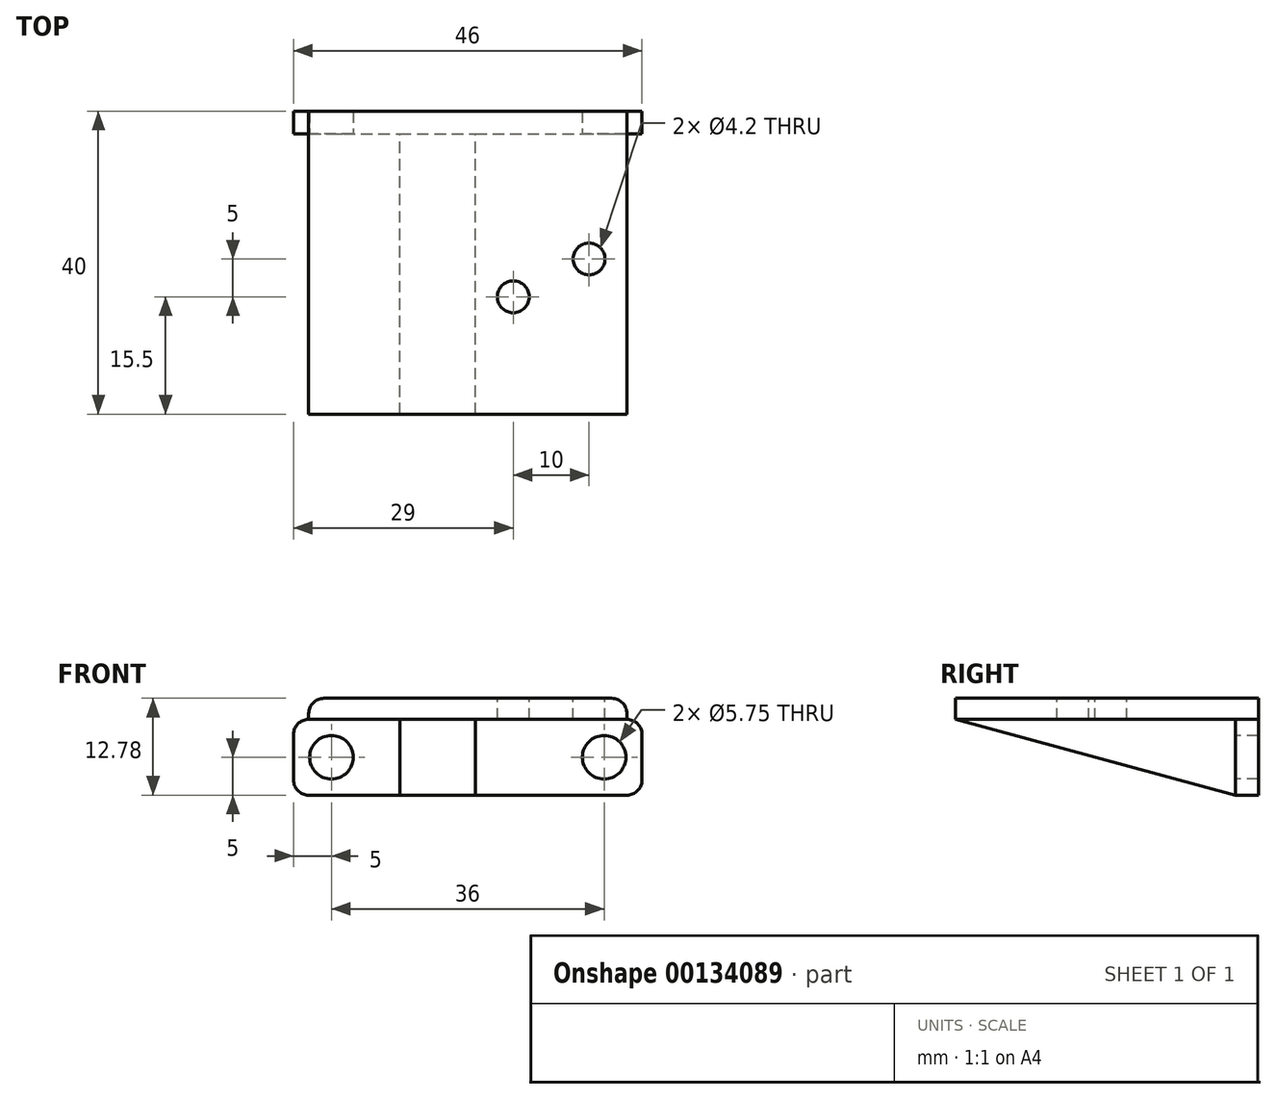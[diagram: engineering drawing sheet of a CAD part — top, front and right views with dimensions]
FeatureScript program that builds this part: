
annotation { "Feature Type Name" : "Feature", "Feature Type Description" : "" }
export const myFeature = defineFeature(function(context is Context, id is Id, definition is map)
    precondition{}
    {
        {
            var Q0;
            Q0=qCreatedBy(makeId("Front.planeOp"),FACE);
            var sketch = newSketch(context, id + "F0", { "sketchPlane" : qUnion([Q0])});
            skLineSegment(sketch, "E0.bottom", {"start": v(-21, 0) * mm, "end": v(21, 0) * mm});
            skLineSegment(sketch, "E0.top", {"start": v(-21, -10) * mm, "end": v(21, -10) * mm});
            skLineSegment(sketch, "E0.left", {"start": v(-23, -2) * mm, "end": v(-23, -8) * mm});
            skLineSegment(sketch, "E0.right", {"start": v(23, -2) * mm, "end": v(23, -8) * mm});
            skLineSegment(sketch, "E1", {"start": v(-23, 0) * mm, "end": v(0, 0) * mm, "construction": true});
            skLineSegment(sketch, "E2", {"start": v(0, 0) * mm, "end": v(23, 0) * mm, "construction": true});
            skPoint(sketch, "E3.visualSharp", {"position": v(-23, 0) * mm});
            skArc(sketch, "E3.filletArc", {"start": v(-21, 0) * mm, "mid": v(-22.41, -0.59) * mm, "end": v(-23, -2) * mm});
            skPoint(sketch, "E4.visualSharp", {"position": v(23, 0) * mm});
            skArc(sketch, "E4.filletArc", {"start": v(23, -2) * mm, "mid": v(22.41, -0.59) * mm, "end": v(21, 0) * mm});
            skPoint(sketch, "E5.visualSharp", {"position": v(23, -10) * mm});
            skArc(sketch, "E5.filletArc", {"start": v(21, -10) * mm, "mid": v(22.41, -9.41) * mm, "end": v(23, -8) * mm});
            skPoint(sketch, "E6.visualSharp", {"position": v(-23, -10) * mm});
            skArc(sketch, "E6.filletArc", {"start": v(-23, -8) * mm, "mid": v(-22.41, -9.41) * mm, "end": v(-21, -10) * mm});
            skPoint(sketch, "E7.endSnap0", {"position": v(0, -10) * mm});
            skSolve(sketch);
        }
        {
            var Q0;
            Q0 = qSketchRegion(id + "F0", true);
            extrude(context, id + "F1", {"entities" : qUnion([Q0]), "depth" : 3 * mm});
        }
        {
            var Q0;
            Q0=makeQuery(id+"F1.opExtrude","CAP_FACE",FACE,{"disambiguationData":[OSD([sQuery(id+"F0.wireOp",EDGE,"E0.bottom"),sQuery(id+"F0.wireOp",EDGE,"E0.top"),sQuery(id+"F0.wireOp",EDGE,"E0.left"),sQuery(id+"F0.wireOp",EDGE,"E0.right"),sQuery(id+"F0.wireOp",EDGE,"E3.filletArc"),sQuery(id+"F0.wireOp",EDGE,"E4.filletArc"),sQuery(id+"F0.wireOp",EDGE,"E5.filletArc"),sQuery(id+"F0.wireOp",EDGE,"E6.filletArc")])],"isStart":false});
            var sketch = newSketch(context, id + "F2", { "sketchPlane" : qUnion([Q0])});
            skLineSegment(sketch, "E8", {"start": v(0, 0) * mm, "end": v(0, -5) * mm, "construction": true});
            skLineSegment(sketch, "E9", {"start": v(0, -5) * mm, "end": v(0, -10) * mm, "construction": true});
            skLineSegment(sketch, "E10", {"start": v(-18, -5) * mm, "end": v(0, -5) * mm, "construction": true});
            skLineSegment(sketch, "E11", {"start": v(0, -5) * mm, "end": v(18, -5) * mm, "construction": true});
            skCircle(sketch, "E12", {"center": v(-18, -5) * mm, "radius": 2.88 * mm});
            skCircle(sketch, "E13", {"center": v(18, -5) * mm, "radius": 2.88 * mm});
            skSolve(sketch);
        }
        {
            var Q0;
            Q0 = qSketchRegion(id + "F2", true);
            extrude(context, id + "F3", {"entities" : qUnion([Q0]), "operationType" : NewBodyOperationType.REMOVE, "oppositeDirection" : true, "depth" : 25 * mm});
        }
        {
            var Q0;
            Q0=makeQuery(id+"F1.opExtrude","CAP_FACE",FACE,{"disambiguationData":[OSD([sQuery(id+"F0.wireOp",EDGE,"E0.bottom"),sQuery(id+"F0.wireOp",EDGE,"E0.top"),sQuery(id+"F0.wireOp",EDGE,"E0.left"),sQuery(id+"F0.wireOp",EDGE,"E0.right"),sQuery(id+"F0.wireOp",EDGE,"E3.filletArc"),sQuery(id+"F0.wireOp",EDGE,"E4.filletArc"),sQuery(id+"F0.wireOp",EDGE,"E5.filletArc"),sQuery(id+"F0.wireOp",EDGE,"E6.filletArc")])],"isStart":false});
            var sketch = newSketch(context, id + "F4", { "sketchPlane" : qUnion([Q0])});
            skLineSegment(sketch, "E14.bottom", {"start": v(-21, 0) * mm, "end": v(21, 0) * mm});
            skLineSegment(sketch, "E14.top", {"start": v(-19, 2.78) * mm, "end": v(19, 2.78) * mm});
            skLineSegment(sketch, "E14.left", {"start": v(-21, 0) * mm, "end": v(-21, 0.78) * mm});
            skLineSegment(sketch, "E14.right", {"start": v(21, 0) * mm, "end": v(21, 0.78) * mm});
            skLineSegment(sketch, "E15.bottom", {"start": v(-9, 0) * mm, "end": v(1, 0) * mm});
            skLineSegment(sketch, "E15.top", {"start": v(-9, -10) * mm, "end": v(1, -10) * mm});
            skLineSegment(sketch, "E15.left", {"start": v(-9, 0) * mm, "end": v(-9, -10) * mm});
            skLineSegment(sketch, "E15.right", {"start": v(1, 0) * mm, "end": v(1, -10) * mm});
            skPoint(sketch, "E16.visualSharp", {"position": v(-21, 2.78) * mm});
            skArc(sketch, "E16.filletArc", {"start": v(-19, 2.78) * mm, "mid": v(-20.41, 2.2) * mm, "end": v(-21, 0.78) * mm});
            skPoint(sketch, "E17.visualSharp", {"position": v(21, 2.78) * mm});
            skArc(sketch, "E17.filletArc", {"start": v(21, 0.78) * mm, "mid": v(20.41, 2.2) * mm, "end": v(19, 2.78) * mm});
            skLineSegment(sketch, "E18", {"start": v(1, -5) * mm, "end": v(23, -5) * mm, "construction": true});
            skLineSegment(sketch, "E19", {"start": v(1, -5) * mm, "end": v(-9, -5) * mm, "construction": true});
            skSolve(sketch);
        }
        {
            var Q0;
            Q0 = qSketchRegion(id + "F4", true);
            extrude(context, id + "F5", {"entities" : qUnion([Q0]), "operationType" : NewBodyOperationType.ADD, "depth" : 37 * mm, "hasSecondDirection" : true, "secondDirectionOppositeDirection" : true, "secondDirectionDepth" : 3 * mm});
        }
        {
            var Q0;
            Q0=makeQuery(id+"F5.opExtrude","SWEPT_FACE",FACE,{"disambiguationData":[OSD([sQuery(id+"F4.wireOp",EDGE,"E15.right")])]});
            var sketch = newSketch(context, id + "F6", { "sketchPlane" : qUnion([Q0])});
            skLineSegment(sketch, "E20", {"start": v(-40, 0) * mm, "end": v(-3, -10) * mm});
            skLineSegment(sketch, "E21", {"start": v(-40, 0) * mm, "end": v(-40, -10) * mm});
            skLineSegment(sketch, "E22", {"start": v(-40, -10) * mm, "end": v(-3, -10) * mm});
            skSolve(sketch);
        }
        {
            var Q0;
            Q0 = qSketchRegion(id + "F6", true);
            extrude(context, id + "F7", {"entities" : qUnion([Q0]), "operationType" : NewBodyOperationType.REMOVE, "oppositeDirection" : true, "depth" : 25 * mm});
        }
        {
            var Q0;
            Q0=makeQuery(id+"F5.opExtrude","SWEPT_FACE",FACE,{"disambiguationData":[OSD([sQuery(id+"F4.wireOp",EDGE,"E14.top")])]});
            var sketch = newSketch(context, id + "F8", { "sketchPlane" : qUnion([Q0])});
            skLineSegment(sketch, "E23.bottom", {"start": v(16, -19.5) * mm, "end": v(6, -19.5) * mm, "construction": true});
            skLineSegment(sketch, "E23.top", {"start": v(16, -24.5) * mm, "end": v(6, -24.5) * mm, "construction": true});
            skLineSegment(sketch, "E23.left", {"start": v(16, -19.5) * mm, "end": v(16, -24.5) * mm, "construction": true});
            skLineSegment(sketch, "E23.right", {"start": v(6, -19.5) * mm, "end": v(6, -24.5) * mm, "construction": true});
            skLineSegment(sketch, "E24", {"start": v(11, -19.5) * mm, "end": v(11, -22) * mm, "construction": true});
            skLineSegment(sketch, "E25", {"start": v(11, -22) * mm, "end": v(11, -24.5) * mm, "construction": true});
            skLineSegment(sketch, "E26", {"start": v(16, -22) * mm, "end": v(11, -22) * mm, "construction": true});
            skPoint(sketch, "E26.endSnap0", {"position": v(11, -23.25) * mm});
            skLineSegment(sketch, "E27", {"start": v(11, -22) * mm, "end": v(6, -22) * mm, "construction": true});
            skCircle(sketch, "E28", {"center": v(16, -19.5) * mm, "radius": 2.1 * mm});
            skCircle(sketch, "E29", {"center": v(6, -24.5) * mm, "radius": 2.1 * mm});
            skLineSegment(sketch, "E30", {"start": v(11, -22) * mm, "end": v(19, -22) * mm, "construction": true});
            skLineSegment(sketch, "E31", {"start": v(11, -22) * mm, "end": v(11, 0) * mm, "construction": true});
            skSolve(sketch);
        }
        {
            var Q0;
            Q0 = qSketchRegion(id + "F8", true);
            extrude(context, id + "F9", {"entities" : qUnion([Q0]), "operationType" : NewBodyOperationType.REMOVE, "oppositeDirection" : true, "depth" : 25 * mm});
        }
    });
